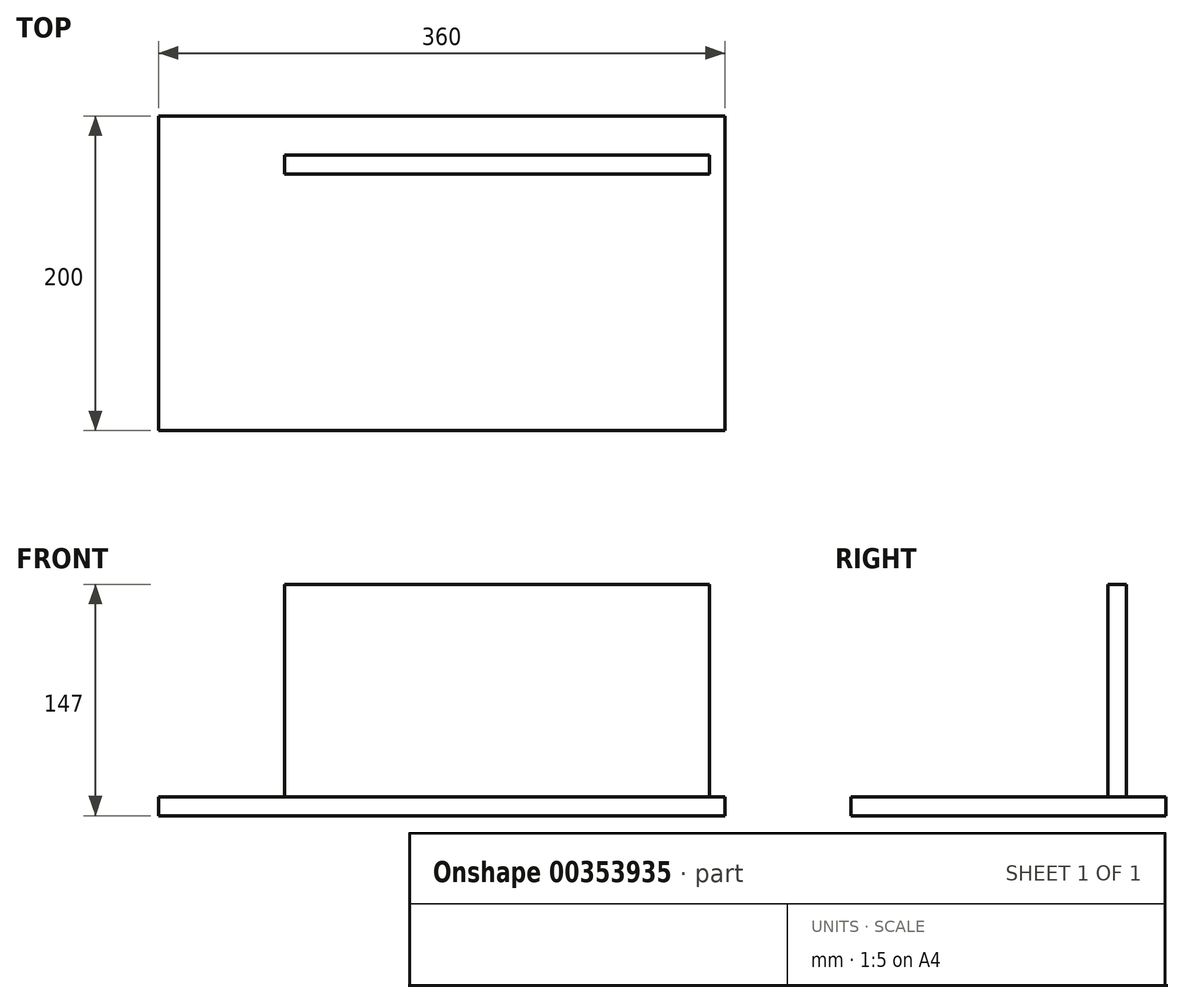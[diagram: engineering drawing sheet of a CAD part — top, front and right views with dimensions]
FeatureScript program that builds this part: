
annotation { "Feature Type Name" : "Feature", "Feature Type Description" : "" }
export const myFeature = defineFeature(function(context is Context, id is Id, definition is map)
    precondition{}
    {
        {
            var Q0;
            Q0=qCreatedBy(makeId("Top.planeOp"),FACE);
            var sketch = newSketch(context, id + "F0", { "sketchPlane" : qUnion([Q0])});
            skLineSegment(sketch, "E0", {"start": v(0, 0) * mm, "end": v(360, 0) * mm});
            skLineSegment(sketch, "E1", {"start": v(360, 0) * mm, "end": v(360, -200) * mm});
            skLineSegment(sketch, "E2", {"start": v(360, -200) * mm, "end": v(0, -200) * mm});
            skLineSegment(sketch, "E3", {"start": v(0, -200) * mm, "end": v(0, 0) * mm});
            skSolve(sketch);
        }
        {
            var Q0;
            Q0=makeQuery(id+"F0.imprint","IMPRINT",FACE,{"disambiguationData":[TD([[makeQuery(id+"F0.imprint","IMPRINT",EDGE,{"derivedFrom":sQuery(id+"F0.wireOp",EDGE,"E0")}),-1.0]])]});
            extrude(context, id + "F1", {"entities" : qUnion([Q0]), "depth" : 12 * mm});
        }
        {
            var Q0;
            Q0=makeQuery(id+"F1.opExtrude","CAP_FACE",FACE,{"disambiguationData":[OSD([sQuery(id+"F0.wireOp",EDGE,"E0"),sQuery(id+"F0.wireOp",EDGE,"E1"),sQuery(id+"F0.wireOp",EDGE,"E2"),sQuery(id+"F0.wireOp",EDGE,"E3")])],"isStart":false});
            var sketch = newSketch(context, id + "F2", { "sketchPlane" : qUnion([Q0])});
            skLineSegment(sketch, "E4", {"start": v(0, 0) * mm, "end": v(80, 0) * mm, "construction": true});
            skLineSegment(sketch, "E5", {"start": v(80, 0) * mm, "end": v(80, -25) * mm, "construction": true});
            skLineSegment(sketch, "E6", {"start": v(80, -25) * mm, "end": v(350, -25) * mm});
            skLineSegment(sketch, "E7", {"start": v(350, -25) * mm, "end": v(350, -37) * mm});
            skLineSegment(sketch, "E8", {"start": v(350, -37) * mm, "end": v(80, -37) * mm});
            skLineSegment(sketch, "E9", {"start": v(80, -37) * mm, "end": v(80, -25) * mm});
            skSolve(sketch);
        }
        {
            var Q0;
            Q0=makeQuery(id+"F2.imprint","IMPRINT",FACE,{"disambiguationData":[TD([[makeQuery(id+"F2.imprint","IMPRINT",EDGE,{"derivedFrom":sQuery(id+"F2.wireOp",EDGE,"E6")}),-1.0]])]});
            extrude(context, id + "F3", {"entities" : qUnion([Q0]), "depth" : 135 * mm});
        }
    });
